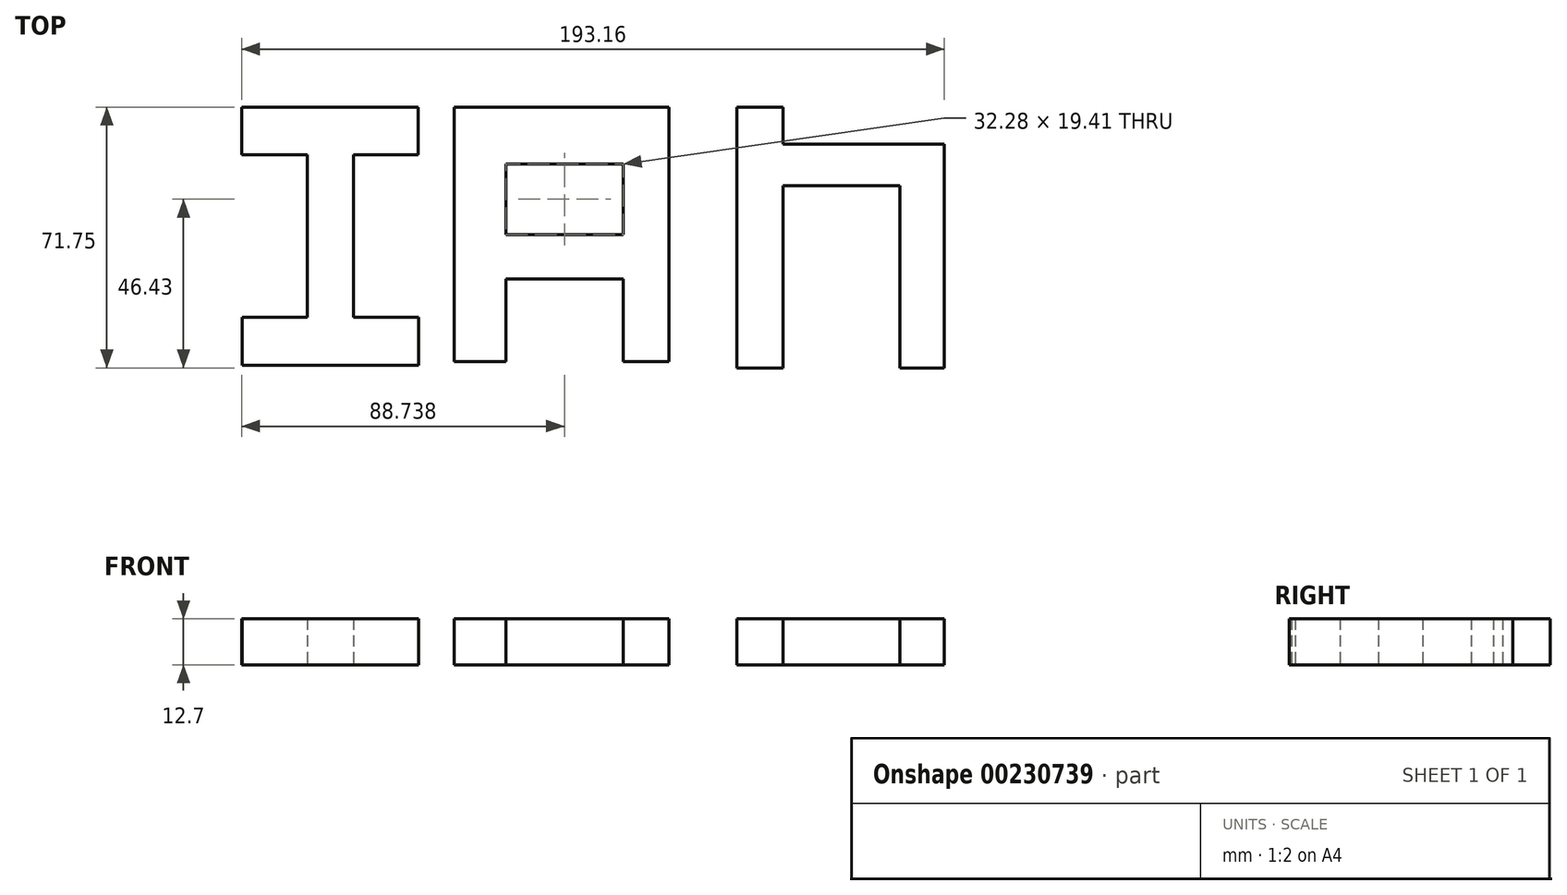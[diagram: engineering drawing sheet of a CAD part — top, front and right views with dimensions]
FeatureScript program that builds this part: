
annotation { "Feature Type Name" : "Feature", "Feature Type Description" : "" }
export const myFeature = defineFeature(function(context is Context, id is Id, definition is map)
    precondition{}
    {
        {
            var Q0;
            Q0=qCreatedBy(makeId("Top.planeOp"),FACE);
            var sketch = newSketch(context, id + "F0", { "sketchPlane" : qUnion([Q0])});
            skLineSegment(sketch, "E0.bottom", {"start": v(-99.67, 27.6) * mm, "end": v(-51.13, 27.6) * mm});
            skLineSegment(sketch, "E0.top", {"start": v(-99.67, 14.49) * mm, "end": v(-51.13, 14.49) * mm});
            skLineSegment(sketch, "E0.left", {"start": v(-99.67, 27.6) * mm, "end": v(-99.67, 14.49) * mm});
            skLineSegment(sketch, "E0.right", {"start": v(-51.13, 27.6) * mm, "end": v(-51.13, 14.49) * mm});
            skLineSegment(sketch, "E1.bottom", {"start": v(-99.57, -30.18) * mm, "end": v(-51.03, -30.18) * mm});
            skLineSegment(sketch, "E1.top", {"start": v(-99.57, -43.47) * mm, "end": v(-51.03, -43.47) * mm});
            skLineSegment(sketch, "E1.left", {"start": v(-99.57, -30.18) * mm, "end": v(-99.57, -43.47) * mm});
            skLineSegment(sketch, "E1.right", {"start": v(-51.03, -30.18) * mm, "end": v(-51.03, -43.47) * mm});
            skLineSegment(sketch, "E2.bottom", {"start": v(-81.7, 14.49) * mm, "end": v(-68.98, 14.49) * mm});
            skLineSegment(sketch, "E2.top", {"start": v(-81.7, -30.18) * mm, "end": v(-68.98, -30.18) * mm});
            skLineSegment(sketch, "E2.left", {"start": v(-81.7, 14.49) * mm, "end": v(-81.7, -30.18) * mm});
            skLineSegment(sketch, "E2.right", {"start": v(-68.98, 14.49) * mm, "end": v(-68.98, -30.18) * mm});
            skLineSegment(sketch, "E3.bottom", {"start": v(-41.2, 27.6) * mm, "end": v(17.78, 27.6) * mm});
            skLineSegment(sketch, "E3.top", {"start": v(-41.2, -42.46) * mm, "end": v(-27.07, -42.46) * mm});
            skLineSegment(sketch, "E3.left", {"start": v(-41.2, 27.6) * mm, "end": v(-41.2, -42.46) * mm});
            skLineSegment(sketch, "E3.right", {"start": v(17.78, 27.6) * mm, "end": v(17.78, -42.46) * mm});
            skLineSegment(sketch, "E4.top", {"start": v(-27.07, 11.97) * mm, "end": v(5.2, 11.97) * mm});
            skLineSegment(sketch, "E4.left", {"start": v(-27.07, -42.46) * mm, "end": v(-27.07, 11.97) * mm});
            skLineSegment(sketch, "E4.right", {"start": v(5.2, -42.46) * mm, "end": v(5.2, 11.97) * mm});
            skLineSegment(sketch, "E5.bottom", {"start": v(-41.2, -7.43) * mm, "end": v(17.78, -7.43) * mm});
            skLineSegment(sketch, "E5.top", {"start": v(-41.2, -19.67) * mm, "end": v(17.78, -19.67) * mm});
            skLineSegment(sketch, "E5.left", {"start": v(-41.2, -7.43) * mm, "end": v(-41.2, -19.67) * mm});
            skLineSegment(sketch, "E5.right", {"start": v(17.78, -7.43) * mm, "end": v(17.78, -19.67) * mm});
            skLineSegment(sketch, "E6.trimOffspring", {"start": v(5.2, -42.46) * mm, "end": v(17.78, -42.46) * mm});
            skLineSegment(sketch, "E7", {"start": v(-51.13, 27.6) * mm, "end": v(124.1, 27.6) * mm});
            skLineSegment(sketch, "E8.bottom", {"start": v(36.48, 27.6) * mm, "end": v(49.19, 27.6) * mm});
            skLineSegment(sketch, "E8.top", {"start": v(36.48, -44.16) * mm, "end": v(49.19, -44.16) * mm});
            skLineSegment(sketch, "E8.left", {"start": v(36.48, 27.6) * mm, "end": v(36.48, -44.16) * mm});
            skLineSegment(sketch, "E8.right", {"start": v(49.19, 27.6) * mm, "end": v(49.19, -44.16) * mm});
            skLineSegment(sketch, "E9.bottom", {"start": v(36.48, 17.34) * mm, "end": v(93.49, 17.34) * mm});
            skLineSegment(sketch, "E9.top", {"start": v(36.48, 5.98) * mm, "end": v(93.49, 5.98) * mm});
            skLineSegment(sketch, "E9.left", {"start": v(36.48, 17.34) * mm, "end": v(36.48, 5.98) * mm});
            skLineSegment(sketch, "E9.right", {"start": v(93.49, 17.34) * mm, "end": v(93.49, 5.98) * mm});
            skLineSegment(sketch, "E10.bottom", {"start": v(81.25, 5.98) * mm, "end": v(93.49, 5.98) * mm});
            skLineSegment(sketch, "E10.top", {"start": v(81.25, -44.16) * mm, "end": v(93.49, -44.16) * mm});
            skLineSegment(sketch, "E10.left", {"start": v(81.25, 5.98) * mm, "end": v(81.25, -44.16) * mm});
            skLineSegment(sketch, "E10.right", {"start": v(93.49, 5.98) * mm, "end": v(93.49, -44.16) * mm});
            skSolve(sketch);
        }
        {
            var Q0;
            Q0 = qSketchRegion(id + "F0", true);
            extrude(context, id + "F1", {"entities" : qUnion([Q0]), "depth" : 12.7 * mm});
        }
    });
